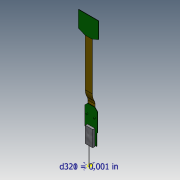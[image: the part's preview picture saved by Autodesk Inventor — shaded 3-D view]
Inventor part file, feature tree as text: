
AUTODESK INVENTOR PART (.ipt)
format: ipt  version: 2018.3 (Build 223284000, 284)  size: 1,059,328 bytes
history: native  units: in
note: dims shown in document units (in); Inventor stores cm internally (conversion verified against a paired STEP export)
features: sketch x9, extrude x6, plane x3, other x3, projected_geometry x3
ambient origin geometry x8: Origin, YZ Plane, XZ Plane, XY Plane, X Axis, Y Axis, Z Axis, Center Point
bodies: Body1 (feature_tree)
feature tree (24):
  sketch  "Sketch1"  dims[d175=0.3937in d243=0.73in]
  plane  "Work Plane4"
  extrude  "Extrusion4"  Depth=0.73in
  sketch  "Sketch3"  dims[d244=0.365in d245=0.28in]
  plane  "Work Plane1"
  sketch  "Sketch4"  dims[d246=0.155in d247=0.46in]
  plane  "Work Plane2"
  extrude  "Extrusion11"  Depth=0.28in
  sketch  "Sketch9"  dims[d268=0.357in]
  extrude  "Extrusion8"  Depth=0.46in
  extrude  "Extrusion9"  Depth=1.335in
  extrude  "Extrusion10"  Depth=0.442in
  extrude  "Extrusion12"  Depth=0.417in
  sketch  "Sketch11"  dims[d277=0.007in d283=0.165in d284=0.02in d285=0.35in d286=0.048in d287=0.0in d288=0.0028in d289=0.0028in d290=0.3937in d291=0.0in d292=0.1685in d294=0.0842in d295=0.033in d296=0.02in d297=0.0in d298=0.0295in d299=0.008in d300=0.0in d301=1.725in d307=0.7734in d308=0.417in d312=0.1575in d313=0.0in d314=0.2in d318=0.06in d320=0.0014in d321=0.0014in]
  other  "Work Point1"
  other  "Image3"
  other  "Image4"
  sketch  "Sketch6"  dims[d252=0.008in d253=0.0in d263=1.335in]
  sketch  "Sketch7"  dims[d264=0.153in d265=0.442in]
  projected_geometry  "Projected Loop1"
  sketch  "Sketch8"  dims[d266=0.221in d267=0.417in]
  projected_geometry  "Projected Loop2"
  sketch  "Sketch10"  dims[d269=0.357in]
  projected_geometry  "Projected Loop3"
